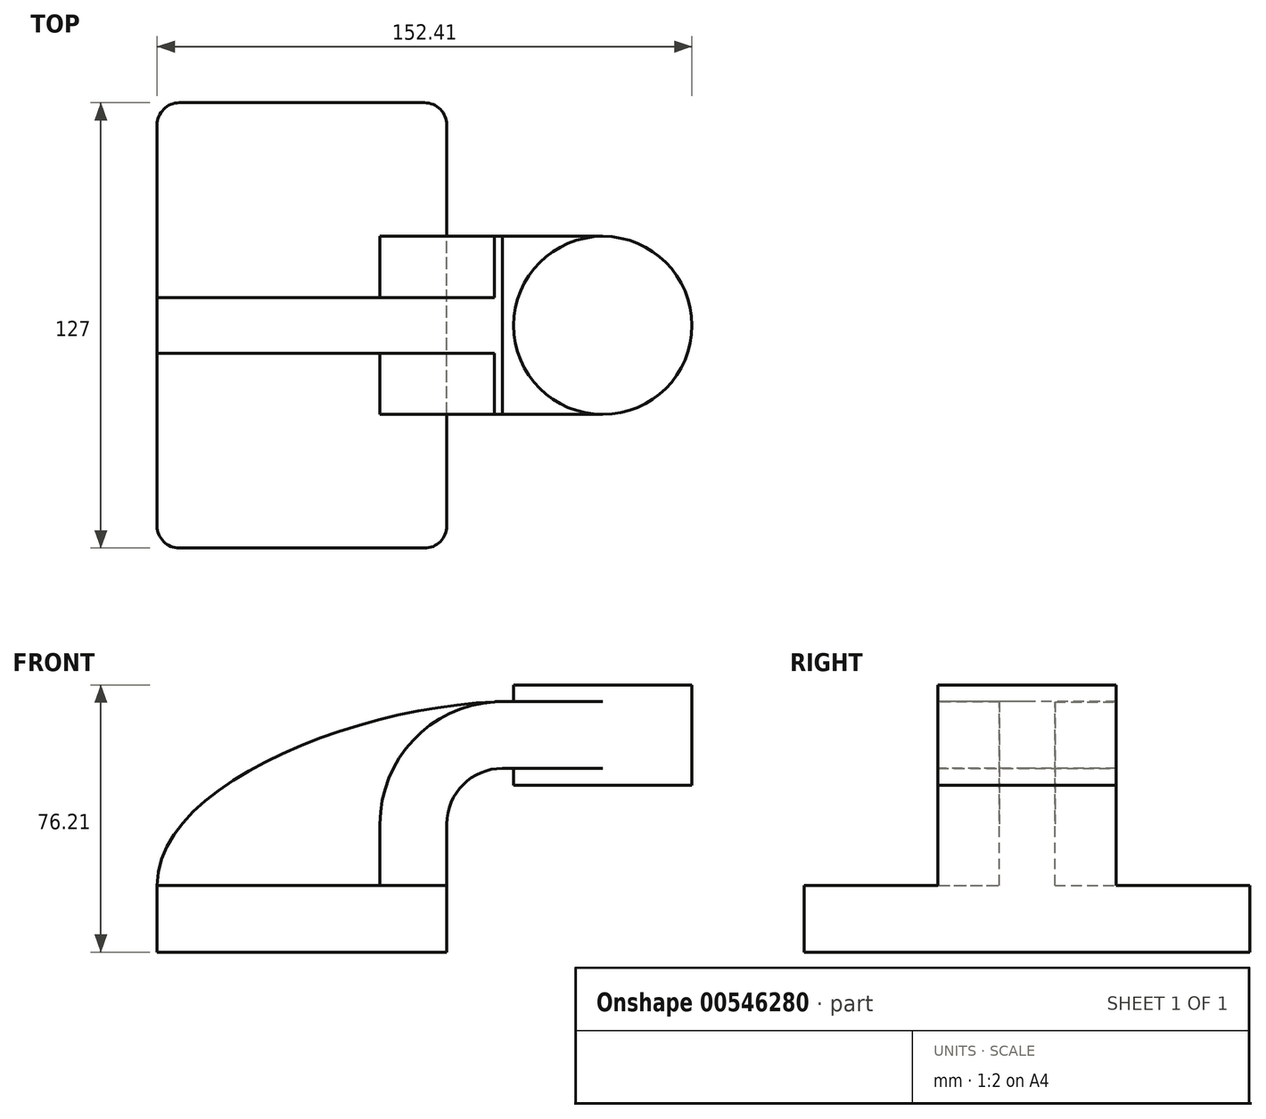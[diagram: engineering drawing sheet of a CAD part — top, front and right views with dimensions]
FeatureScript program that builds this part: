
annotation { "Feature Type Name" : "Feature", "Feature Type Description" : "" }
export const myFeature = defineFeature(function(context is Context, id is Id, definition is map)
    precondition{}
    {
        {
            var Q0;
            Q0=qCreatedBy(makeId("Front.planeOp"),FACE);
            var sketch = newSketch(context, id + "F0", { "sketchPlane" : qUnion([Q0])});
            skLineSegment(sketch, "E0.bottom", {"start": v(-41.28, 9.52) * mm, "end": v(41.28, 9.52) * mm});
            skLineSegment(sketch, "E0.top", {"start": v(-41.28, -9.53) * mm, "end": v(41.28, -9.53) * mm});
            skLineSegment(sketch, "E0.left", {"start": v(-41.28, 9.52) * mm, "end": v(-41.28, -9.53) * mm});
            skLineSegment(sketch, "E0.right", {"start": v(41.28, 9.52) * mm, "end": v(41.28, -9.52) * mm});
            skPoint(sketch, "E0.middle", {"position": v(0, 0) * mm});
            skLineSegment(sketch, "E1.bottom", {"start": v(111.12, 38.1) * mm, "end": v(60.32, 38.1) * mm});
            skLineSegment(sketch, "E1.top", {"start": v(111.12, 66.68) * mm, "end": v(60.32, 66.68) * mm});
            skLineSegment(sketch, "E1.left", {"start": v(111.12, 38.1) * mm, "end": v(111.12, 66.68) * mm});
            skLineSegment(sketch, "E1.right", {"start": v(60.32, 38.1) * mm, "end": v(60.32, 66.68) * mm});
            skPoint(sketch, "E1.middle", {"position": v(85.73, 52.39) * mm});
            skLineSegment(sketch, "E2", {"start": v(41.28, 9.52) * mm, "end": v(41.28, 27) * mm});
            skArc(sketch, "E3", {"start": v(41.28, 27) * mm, "mid": v(45.92, 38.23) * mm, "end": v(57.15, 42.88) * mm});
            skLineSegment(sketch, "E4", {"start": v(57.15, 42.88) * mm, "end": v(85.72, 42.88) * mm});
            skPoint(sketch, "E4.endSnap0", {"position": v(85.72, 66.68) * mm});
            skLineSegment(sketch, "E5.0", {"start": v(57.15, 61.93) * mm, "end": v(85.72, 61.93) * mm});
            skArc(sketch, "E5.1", {"start": v(22.23, 27) * mm, "mid": v(32.45, 51.7) * mm, "end": v(57.15, 61.93) * mm});
            skLineSegment(sketch, "E5.2", {"start": v(22.23, 9.52) * mm, "end": v(22.23, 27) * mm});
            skLineSegment(sketch, "E6", {"start": v(85.72, 38.1) * mm, "end": v(85.72, 66.68) * mm});
            skFitSpline(sketch, "E7", {"points": [v(-41.28, 9.52) * mm, v(57.15, 61.93) * mm], "startDerivative": vector(0.2, 88.66) * mm, "endDerivative": vector(118.47, 2.72) * mm});
            skSolve(sketch);
        }
        {
            var Q0;
            Q0=makeQuery(id+"F0.imprint","IMPRINT",FACE,{"disambiguationData":[TD([[makeQuery(id+"F0.imprint","IMPRINT",EDGE,{"derivedFrom":sQuery(id+"F0.wireOp",EDGE,"E0.top")}),1.0]])]});
            extrude(context, id + "F1", {"entities" : qUnion([Q0]), "endBound" : BoundingType.SYMMETRIC, "depth" : 127 * mm, "offsetDistance" : 25.4 * mm});
        }
        {
            var Q0;
            {var subQ1=sQuery(id+"F0.wireOp",EDGE,"E2");Q0=makeQuery(id+"F0.imprint","IMPRINT",FACE,{"disambiguationData":[TD([[makeQuery(id+"F0.imprint","IMPRINT",EDGE,{"derivedFrom":subQ1}),1.0]])]});}
            var Q1;
            {var subQ0=sQuery(id+"F0.wireOp",EDGE,"E4");var subQ1=sQuery(id+"F0.wireOp",EDGE,"E1.right");var subQ2=makeQuery(id+"F0.imprint","INTERSECT",VERTEX,{"derivedFrom":[subQ1,subQ0]});Q1=makeQuery(id+"F0.imprint","IMPRINT",FACE,{"disambiguationData":[TD([[makeQuery(id+"F0.imprint","IMPRINT",EDGE,{"disambiguationData":[TD([[subQ2,-1.0]])],"derivedFrom":subQ1}),-1.0]])]});}
            extrude(context, id + "F2", {"entities" : qUnion([Q0, Q1]), "operationType" : NewBodyOperationType.ADD, "endBound" : BoundingType.SYMMETRIC, "depth" : 50.8 * mm, "offsetDistance" : 25.4 * mm});
        }
        {
            var Q0;
            {var subQ3=sQuery(id+"F0.wireOp",EDGE,"E5.2");Q0=makeQuery(id+"F0.imprint","IMPRINT",FACE,{"disambiguationData":[TD([[makeQuery(id+"F0.imprint","IMPRINT",EDGE,{"derivedFrom":subQ3}),1.0]])]});}
            extrude(context, id + "F3", {"entities" : qUnion([Q0]), "operationType" : NewBodyOperationType.ADD, "endBound" : BoundingType.SYMMETRIC, "depth" : 15.88 * mm, "offsetDistance" : 25.4 * mm});
        }
        {
            var Q0;
            {var subQ0=sQuery(id+"F0.wireOp",EDGE,"E1.left");Q0=makeQuery(id+"F0.imprint","IMPRINT",FACE,{"disambiguationData":[TD([[makeQuery(id+"F0.imprint","IMPRINT",EDGE,{"derivedFrom":subQ0}),1.0]])]});}
            var Q1;
            Q1=sQuery(id+"F0.wireOp",EDGE,"E6");
            revolve(context, id + "F4", {"operationType" : NewBodyOperationType.ADD, "entities" : qUnion([Q0]), "axis" : qUnion([Q1]), "revolveType" : RevolveType.FULL});
        }
        {
            var Q0;
            Q0=makeQuery(id+"F1.opExtrude","CAP_EDGE",EDGE,{"disambiguationData":[OSD([sQuery(id+"F0.wireOp",EDGE,"E0.left")])],"isStart":false});
            var Q1;
            Q1=makeQuery(id+"F1.opExtrude","CAP_EDGE",EDGE,{"disambiguationData":[OSD([sQuery(id+"F0.wireOp",EDGE,"E0.right")])],"isStart":false});
            var Q2;
            Q2=makeQuery(id+"F1.opExtrude","CAP_EDGE",EDGE,{"disambiguationData":[OSD([sQuery(id+"F0.wireOp",EDGE,"E0.right")])],"isStart":true});
            var Q3;
            Q3=makeQuery(id+"F1.opExtrude","CAP_EDGE",EDGE,{"disambiguationData":[OSD([sQuery(id+"F0.wireOp",EDGE,"E0.left")])],"isStart":true});
            fillet(context, id + "F5", {"entities" : qUnion([Q0, Q1, Q2, Q3]), "radius" : 6.35 * mm, "tangentPropagation" : true, "allowEdgeOverflow" : false});
        }
    });
